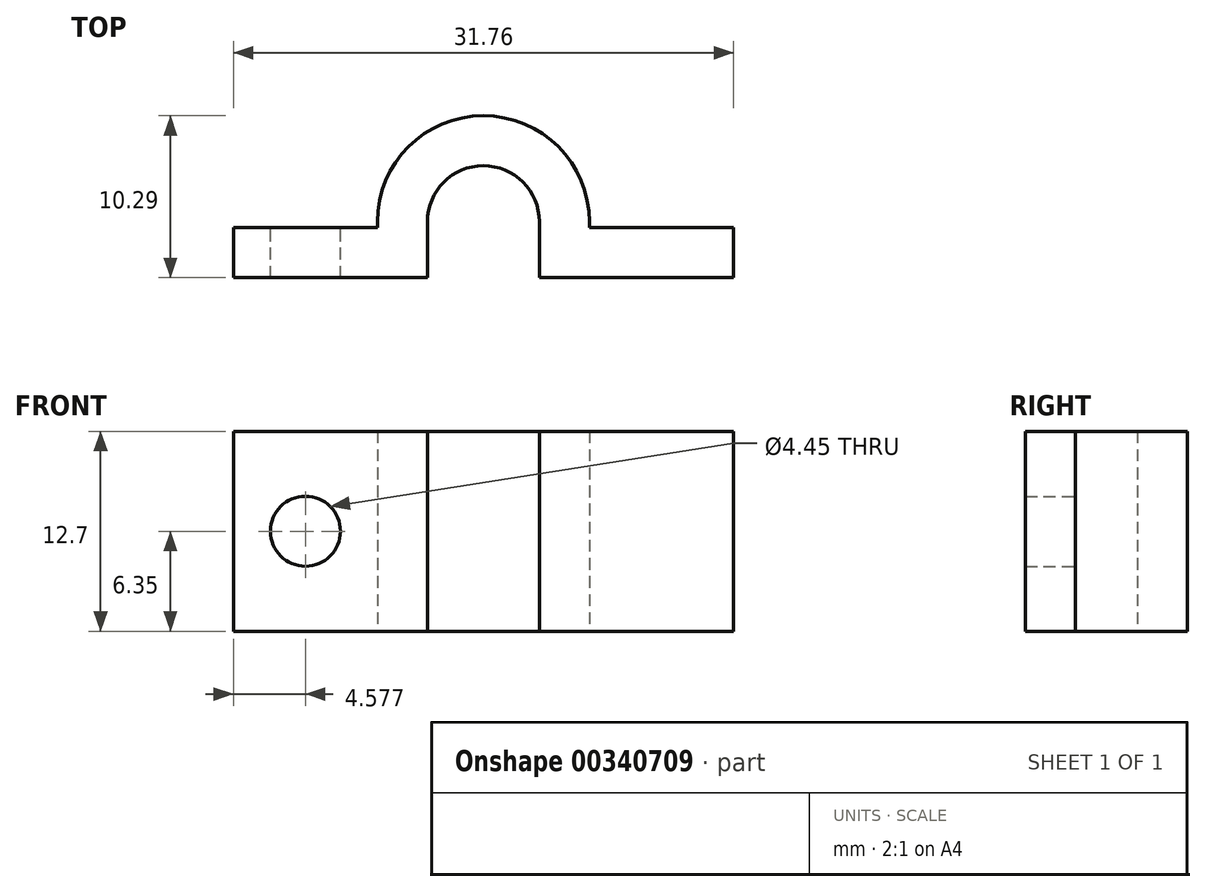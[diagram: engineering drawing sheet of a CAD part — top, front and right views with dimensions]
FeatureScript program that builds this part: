
annotation { "Feature Type Name" : "Feature", "Feature Type Description" : "" }
export const myFeature = defineFeature(function(context is Context, id is Id, definition is map)
    precondition{}
    {
        {
            var Q0;
            Q0=qCreatedBy(makeId("Top.planeOp"),FACE);
            var sketch = newSketch(context, id + "F0", { "sketchPlane" : qUnion([Q0])});
            skLineSegment(sketch, "E0.bottom", {"start": v(-15.87, -0.38) * mm, "end": v(15.87, -0.38) * mm});
            skLineSegment(sketch, "E0.top", {"start": v(-15.87, -3.56) * mm, "end": v(15.87, -3.56) * mm});
            skLineSegment(sketch, "E0.left", {"start": v(-15.87, -0.38) * mm, "end": v(-15.87, -3.56) * mm});
            skLineSegment(sketch, "E0.right", {"start": v(15.88, -0.38) * mm, "end": v(15.88, -3.56) * mm});
            skPoint(sketch, "E1", {"position": v(0, -3.56) * mm});
            skLineSegment(sketch, "E2", {"start": v(-3.56, 0) * mm, "end": v(-3.56, -0.38) * mm});
            skLineSegment(sketch, "E3", {"start": v(3.56, 0) * mm, "end": v(3.56, -0.38) * mm});
            skLineSegment(sketch, "E4", {"start": v(-3.56, -0.38) * mm, "end": v(-3.56, -3.56) * mm});
            skLineSegment(sketch, "E5", {"start": v(3.56, -0.38) * mm, "end": v(3.56, -3.56) * mm});
            skArc(sketch, "E6", {"start": v(-3.56, 0) * mm, "mid": v(0, -3.56) * mm, "end": v(3.56, 0) * mm});
            skArc(sketch, "E7", {"start": v(3.56, 0) * mm, "mid": v(0, 3.56) * mm, "end": v(-3.56, 0) * mm});
            skLineSegment(sketch, "E8.0", {"start": v(-6.73, 0) * mm, "end": v(-6.73, -3.56) * mm});
            skArc(sketch, "E8.1", {"start": v(6.73, 0) * mm, "mid": v(0, 6.73) * mm, "end": v(-6.73, 0) * mm});
            skLineSegment(sketch, "E8.2", {"start": v(6.73, 0) * mm, "end": v(6.73, -3.56) * mm});
            skSolve(sketch);
        }
        {
            var Q0;
            {var subQ0=sQuery(id+"F0.wireOp",EDGE,"E0.left");Q0=makeQuery(id+"F0.imprint","IMPRINT",FACE,{"disambiguationData":[TD([[makeQuery(id+"F0.imprint","IMPRINT",EDGE,{"derivedFrom":subQ0}),1.0]])]});}
            var Q1;
            {var subQ0=sQuery(id+"F0.wireOp",EDGE,"E4");Q1=makeQuery(id+"F0.imprint","IMPRINT",FACE,{"disambiguationData":[TD([[makeQuery(id+"F0.imprint","IMPRINT",EDGE,{"derivedFrom":subQ0}),-1.0]])]});}
            var Q2;
            {var subQ0=sQuery(id+"F0.wireOp",EDGE,"E2");Q2=makeQuery(id+"F0.imprint","IMPRINT",FACE,{"disambiguationData":[TD([[makeQuery(id+"F0.imprint","IMPRINT",EDGE,{"derivedFrom":subQ0}),-1.0]])]});}
            var Q3;
            {var subQ0=sQuery(id+"F0.wireOp",EDGE,"E5");Q3=makeQuery(id+"F0.imprint","IMPRINT",FACE,{"disambiguationData":[TD([[makeQuery(id+"F0.imprint","IMPRINT",EDGE,{"derivedFrom":subQ0}),1.0]])]});}
            var Q4;
            {var subQ0=sQuery(id+"F0.wireOp",EDGE,"E0.right");Q4=makeQuery(id+"F0.imprint","IMPRINT",FACE,{"disambiguationData":[TD([[makeQuery(id+"F0.imprint","IMPRINT",EDGE,{"derivedFrom":subQ0}),-1.0]])]});}
            extrude(context, id + "F1", {"entities" : qUnion([Q0, Q1, Q2, Q3, Q4]), "depth" : 12.7 * mm});
        }
        {
            var Q0;
            {var subQ0=sQuery(id+"F0.wireOp",EDGE,"E0.bottom");Q0=makeQuery(id+"F1.opExtrude","SWEPT_FACE",FACE,{"disambiguationData":[OSD([subQ0]),TDD([makeQuery(id+"F0.imprint","IMPRINT",EDGE,{"disambiguationData":[TD([[makeQuery(id+"F0.imprint","INTERSECT",VERTEX,{"derivedFrom":[subQ0,sQuery(id+"F0.wireOp",EDGE,"E0.left")]}),-1.0]])],"derivedFrom":subQ0})])]});}
            var sketch = newSketch(context, id + "F2", { "sketchPlane" : qUnion([Q0])});
            skCircle(sketch, "E9", {"center": v(11.3, 6.35) * mm, "radius": 2.22 * mm});
            skPoint(sketch, "E9.centerSnap0", {"position": v(15.87, 6.35) * mm});
            skPoint(sketch, "E9.centerSnap1", {"position": v(11.3, 0) * mm});
            skCircle(sketch, "E10.MirrorC", {"center": v(-11.3, 6.35) * mm, "radius": 2.22 * mm});
            skSolve(sketch);
        }
        {
            var Q0;
            Q0=makeQuery(id+"F2.imprint","IMPRINT",FACE,{"disambiguationData":[TD([[makeQuery(id+"F2.imprint","IMPRINT",EDGE,{"derivedFrom":sQuery(id+"F2.wireOp",EDGE,"E9")}),1.0]])]});
            var Q1;
            Q1=makeQuery(id+"F2.imprint","IMPRINT",FACE,{"disambiguationData":[TD([[makeQuery(id+"F2.imprint","IMPRINT",EDGE,{"derivedFrom":sQuery(id+"F2.wireOp",EDGE,"E10.MirrorC")}),-1.0]])]});
            extrude(context, id + "F3", {"entities" : qUnion([Q0, Q1]), "operationType" : NewBodyOperationType.REMOVE, "oppositeDirection" : true, "depth" : 25.4 * mm});
        }
    });
